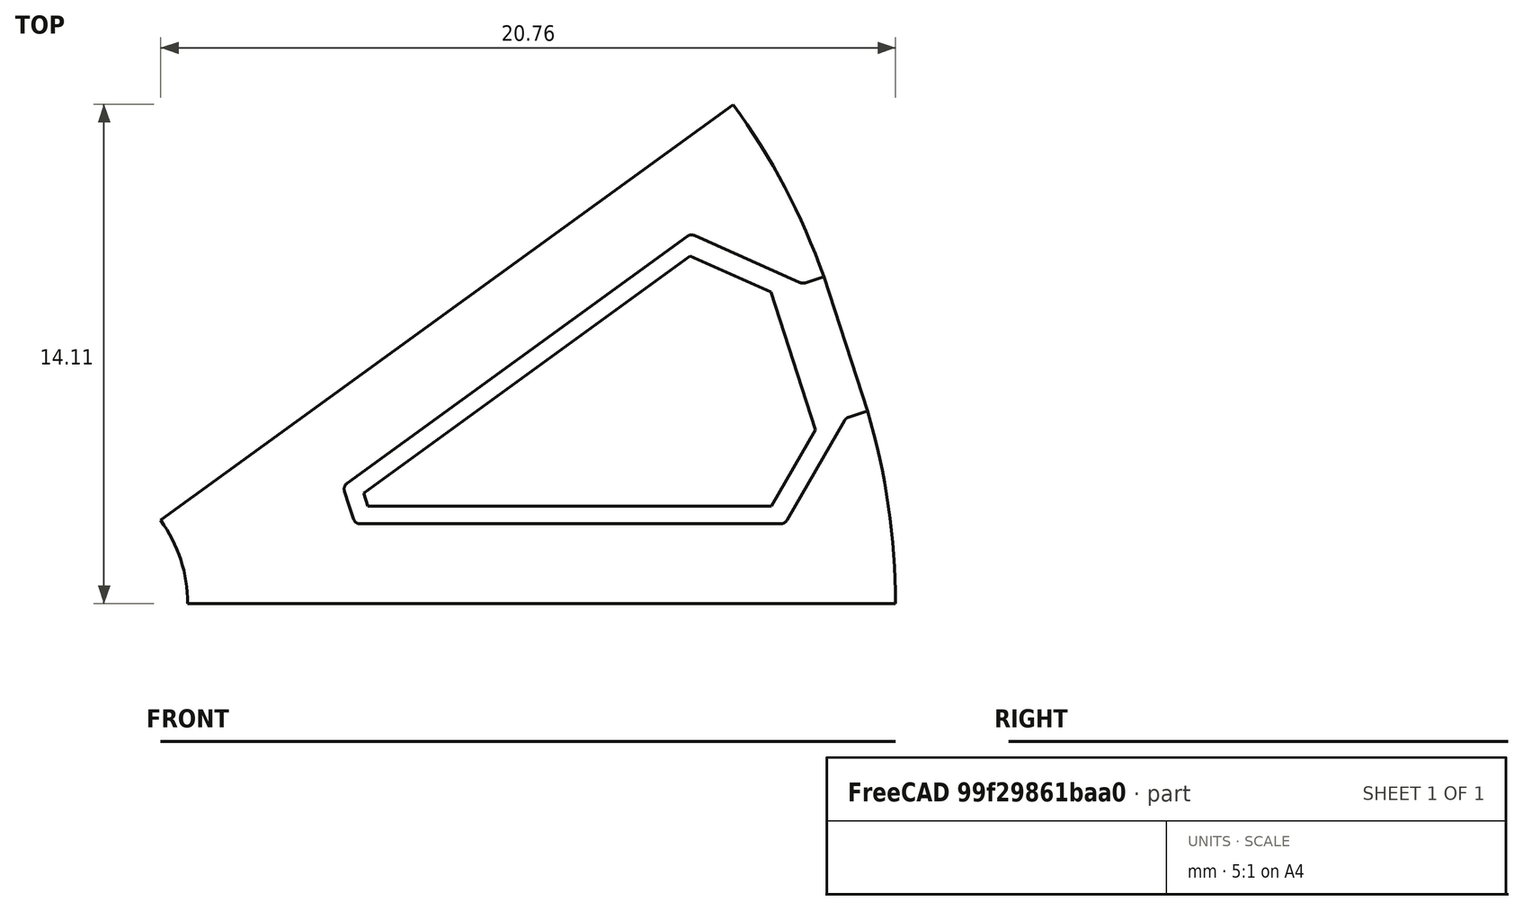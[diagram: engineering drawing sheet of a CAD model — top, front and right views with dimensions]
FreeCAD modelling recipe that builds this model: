
FCSTD DOCUMENT  (FreeCAD 0.18R4 (GitTag))
Label: stator1_new
License: All rights reserved
LicenseURL: http://en.wikipedia.org/wiki/All_rights_reserved
objects: Sketcher::SketchObject×7, Surface::Filling×3, PartDesign::Body×2, Spreadsheet::Sheet×1
note: 12 computed .brp shape members not serialized (recipe doc carries the construction recipe); baked Part::Feature solids carry a one-line shape summary decoded from their .brp

FEATURE [Spreadsheet::Sheet] Spreadsheet  label="Variables"
  cells = A2=slotNumber; B2(slotNumber)=10; A3=outerDiameter; B3(outerDiameter)=48; A4=innerDiameter; B4(innerDiameter)=8; A5=stackLength; B5(stackLength)=26; A6=stackingFactor; B6(stackingFactor)=0.95; A7=cuttingThickness; B7(cuttingThickness)=0.1; A8=skewAngle; B8(skewAngle)=0; A9=segmentAngle; B9(segmentAngle)==360 / slotNumber; A10=tipHeightReduction; B10(tipHeightReduction)=20; A11=toothThickness; B11(toothThickness)=4.5; A12=yokeThickness; B12(yokeThickness)=5; A13=tipHeight; B13(tipHeight)=0.8; A14=tipAngle; B14(tipAngle)=120; A15=openingLeft; B15(openingLeft)=2; A16=openingRight; B16(openingRight)=2; A17=slotIsolation; B17(slotIsolation)=0.5; A18=windingAngle; B18(windingAngle)=35; A19=heightRatio; B19(heightRatio)=40; A20=roundingRadii; B20(roundingRadii)=0.2; A21=coilAxialHeight; B21(coilAxialHeight)=15
FEATURE [Sketcher::SketchObject] Sketch003  label="StatorSketch"
  MapMode = 5
  Support = -> [XY_Plane]
  expr: Constraints[71] = Variables.innerDiameter / 2
  expr: Constraints[26] = Variables.toothThickness / 2
  expr: Constraints[9] = Variables.segmentAngle
  expr: Constraints[27] = Variables.innerDiameter / 2 + Variables.yokeThickness
  expr: Constraints[35] = Variables.roundingRadii
  expr: Constraints[61] = Variables.tipHeight
  expr: Constraints[23] = Variables.tipAngle
  expr: Constraints[16] = Variables.tipHeight * (1 - Variables.tipHeightReduction / 100)
  expr: Constraints[12] = Variables.openingLeft
  expr: Constraints[72] = Variables.segmentAngle / 2
  expr: Constraints[5] = Variables.outerDiameter
  sketch-geometry (29):
    g0: ArcOfCircle [constr] CenterX=0 CenterY=0 CenterZ=0 NormalX=0 NormalY=0 NormalZ=1 AngleXU=0 Radius=24 StartAngle=0 EndAngle=0.628319
    g1: LineSegment [constr] StartX=0 StartY=0 StartZ=0 EndX=19.4164 EndY=14.1068 EndZ=0
    g2: LineSegment [constr] StartX=0 StartY=0 StartZ=0 EndX=24 EndY=-7e-16 EndZ=0
    g3: LineSegment [constr] StartX=0 StartY=0 StartZ=0 EndX=22.8254 EndY=7.41641 EndZ=0
    g4: LineSegment [constr] StartX=15.6745 StartY=18.1744 StartZ=0 EndX=22.1286 EndY=9.29112 EndZ=0
    g5: LineSegment [constr] StartX=22.1286 StartY=9.29112 StartZ=0 EndX=21.4408 EndY=9.06763 EndZ=0
    g6: LineSegment [constr] StartX=21.3678 StartY=9.0439 StartZ=0 EndX=21.9764 EndY=9.24167 EndZ=0
    g7: ArcOfCircle CenterX=3.91276 CenterY=2.84278 CenterZ=0 NormalX=0 NormalY=0 NormalZ=1 AngleXU=0 Radius=19.1636 StartAngle=0.340448 EndAngle=0.628319
    g8: LineSegment StartX=21.2976 StartY=9.07513 StartZ=0 EndX=18.316 EndY=10.4026 EndZ=0
    g9: LineSegment StartX=18.1171 StartY=10.3817 StartZ=0 EndX=8.50448 EndY=3.39772 EndZ=0
    g10: LineSegment StartX=8.43183 StartY=3.17411 StartZ=0 EndX=8.55951 EndY=2.78115 EndZ=0
    g11: LineSegment [constr] StartX=8.50448 StartY=3.39772 StartZ=0 EndX=7.18197 EndY=5.218 EndZ=0
    g12: LineSegment StartX=8.55951 StartY=2.78115 StartZ=0 EndX=8.68719 EndY=2.3882 EndZ=0
    g13: LineSegment StartX=8.8774 StartY=2.25 StartZ=0 EndX=20.7593 EndY=2.25 EndZ=0
    g14: LineSegment StartX=20.9325 StartY=2.35 StartZ=0 EndX=22.5644 EndY=5.17649 EndZ=0
    g15: LineSegment StartX=22.6758 StartY=5.26671 StartZ=0 EndX=23.2114 EndY=5.44075 EndZ=0
    g16: ArcOfCircle CenterX=4.83643 CenterY=-1e-16 CenterZ=0 NormalX=0 NormalY=0 NormalZ=1 AngleXU=0 Radius=19.1636 StartAngle=0 EndAngle=0.287871
    g17: ArcOfCircle CenterX=22.7376 CenterY=5.07649 CenterZ=0 NormalX=0 NormalY=0 NormalZ=1 AngleXU=0 Radius=0.2 StartAngle=1.88496 EndAngle=2.61799
    g18: ArcOfCircle CenterX=20.7593 CenterY=2.45 CenterZ=0 NormalX=0 NormalY=0 NormalZ=1 AngleXU=0 Radius=0.2 StartAngle=4.71239 EndAngle=5.75959
    g19: ArcOfCircle CenterX=8.8774 CenterY=2.45 CenterZ=0 NormalX=0 NormalY=0 NormalZ=1 AngleXU=0 Radius=0.2 StartAngle=3.45575 EndAngle=4.71239
    g20: ArcOfCircle CenterX=18.2347 CenterY=10.2199 CenterZ=0 NormalX=0 NormalY=0 NormalZ=1 AngleXU=0 Radius=0.2 StartAngle=1.15192 EndAngle=2.19911
    g21: ArcOfCircle CenterX=21.379 CenterY=9.25784 CenterZ=0 NormalX=0 NormalY=0 NormalZ=1 AngleXU=0 Radius=0.2 StartAngle=4.29351 EndAngle=5.02655
    g22: ArcOfCircle CenterX=8.62204 CenterY=3.23591 CenterZ=0 NormalX=0 NormalY=0 NormalZ=1 AngleXU=0 Radius=0.2 StartAngle=2.19911 EndAngle=3.45575
    g23: LineSegment [constr] StartX=21.2976 StartY=9.07513 StartZ=0 EndX=21.3678 EndY=9.0439 EndZ=0
    g24: LineSegment [constr] StartX=21.3678 StartY=9.0439 StartZ=0 EndX=21.4408 EndY=9.06763 EndZ=0
    g25: LineSegment StartX=21.4408 StartY=9.06763 StartZ=0 EndX=21.9764 EndY=9.24167 EndZ=0
    g26: LineSegment StartX=19.4164 StartY=14.1068 StartZ=0 EndX=3.23607 EndY=2.35114 EndZ=0
    g27: LineSegment StartX=4 StartY=-1e-16 StartZ=0 EndX=24 EndY=-7e-16 EndZ=0
    g28: ArcOfCircle CenterX=0 CenterY=0 CenterZ=0 NormalX=0 NormalY=0 NormalZ=1 AngleXU=0 Radius=4 StartAngle=0 EndAngle=0.628319
  constraints (73):
    c: Coincident(g0,g-1)
    c: Coincident(g1,g0)
    c: Coincident(g1,g0)
    c: Coincident(g2,g0)
    c: Coincident(g2,g0)
    c: Diameter(g0) = 48
    c: Coincident(g3,g0)
    c: PointOnObject(g3,g0)
    c: Symmetric(g0,g0,g3)
    c: Angle(g2,g1) = 0.628319
    c: PointOnObject(g4,g0)
    c: Symmetric(g4,g4,g1)
    c: Distance(g4,g3) = 2
    c: Coincident(g5,g4)
    c: Parallel(g5,g3)
    c: PointOnObject(g6,g5)
    c: Distance(g6) = 0.64
    c: Coincident(g7,g0)
    c: Coincident(g7,g6)
    c: PointOnObject(g7,g1)
    c: PointOnObject(g10,g3)
    c: Perpendicular(g3,g10)
    c: Parallel(g1,g9)
    c: Angle(g9,g8) = 2.0944
    c: PointOnObject(g11,g1)
    c: Perpendicular(g1,g11)
    c: Distance(g11) = 2.25
    c: Distance(g-1,g10) = 9
    c: Coincident(g12,g10)
    c: Symmetric(g15,g7,g3)
    c: PointOnObject(g16,g2)
    c: Coincident(g16,g0)
    c: Coincident(g16,g15)
    c: Tangent(g14,g17) = 1.5708
    c: Tangent(g15,g17) = 1.5708
    c: Radius(g17) = 0.2
    c: Tangent(g13,g18) = -1.5708
    c: Tangent(g14,g18) = -1.5708
    c: Tangent(g12,g19) = -1.5708
    c: Tangent(g13,g19) = -1.5708
    c: Tangent(g8,g20) = -1.5708
    c: Tangent(g9,g20) = -1.5708
    c: Tangent(g5,g21) = 1.5708
    c: Tangent(g8,g21) = 1.5708
    c: Tangent(g10,g22) = -1.5708
    c: Tangent(g9,g22) = -1.5708
    c: Coincident(g11,g9)
    c: Equal(g17,g18)
    c: Equal(g19,g17)
    c: Equal(g22,g17)
    c: Equal(g20,g17)
    c: Symmetric(g13,g9,g3)
    c: Symmetric(g14,g8,g3)
    c: Symmetric(g14,g8,g3)
    c: Equal(g21,g17)
    c: Coincident(g23,g8)
    c: Coincident(g24,g23)
    c: Coincident(g24,g5)
    c: Parallel(g23,g8)
    c: Parallel(g24,g5)
    c: Coincident(g6,g23)
    c: Distance(g6,g4) = 0.8
    c: Coincident(g25,g21)
    c: Coincident(g25,g7)
    c: Coincident(g26,g7)
    c: PointOnObject(g26,g1)
    c: PointOnObject(g27,g2)
    c: Coincident(g27,g16)
    c: Coincident(g28,g-1)
    c: Coincident(g28,g26)
    c: Coincident(g28,g27)
    c: Radius(g28) = 4
    c: Angle(g-1,g3) = 0.314159
FEATURE [Sketcher::SketchObject] Sketch  label="StatorSide"
  MapMode = 5
  Support = -> [XY_Plane001]
  expr: Constraints[20] = Variables.stackLength
  expr: Constraints[17] = Variables.innerDiameter
  expr: Constraints[16] = Variables.outerDiameter
  sketch-geometry (8):
    g0: LineSegment StartX=-13 StartY=24 StartZ=0 EndX=13 EndY=24 EndZ=0
    g1: LineSegment StartX=13 StartY=24 StartZ=0 EndX=13 EndY=4 EndZ=0
    g2: LineSegment StartX=13 StartY=4 StartZ=0 EndX=-13 EndY=4 EndZ=0
    g3: LineSegment StartX=-13 StartY=4 StartZ=0 EndX=-13 EndY=24 EndZ=0
    g4: LineSegment StartX=-13 StartY=-4 StartZ=0 EndX=13 EndY=-4 EndZ=0
    g5: LineSegment StartX=13 StartY=-4 StartZ=0 EndX=13 EndY=-24 EndZ=0
    g6: LineSegment StartX=13 StartY=-24 StartZ=0 EndX=-13 EndY=-24 EndZ=0
    g7: LineSegment StartX=-13 StartY=-24 StartZ=0 EndX=-13 EndY=-4 EndZ=0
  constraints (21):
    c: Coincident(g0,g1)
    c: Coincident(g1,g2)
    c: Coincident(g2,g3)
    c: Coincident(g3,g0)
    c: Horizontal(g0)
    c: Vertical(g1)
    c: Vertical(g3)
    c: Coincident(g4,g5)
    c: Coincident(g5,g6)
    c: Coincident(g6,g7)
    c: Coincident(g7,g4)
    c: Horizontal(g6)
    c: Vertical(g5)
    c: Vertical(g7)
    c: Symmetric(g2,g1,g-2)
    c: Symmetric(g4,g4,g-2)
    c: DistanceY(g6,g0) = 48
    c: DistanceY(g4,g2) = 8
    c: Symmetric(g4,g2,g-1)
    c: Equal(g7,g3)
    c: DistanceX(g6,g6) = 26
FEATURE [Sketcher::SketchObject] Sketch009  label="WindingSide"
  ExternalGeometry = -> [Sketch]
  MapMode = 5
  Support = -> [XY_Plane001]
  expr: Constraints[18] = Variables.coilAxialHeight
  expr: Constraints[8] = Variables.coilAxialHeight
  sketch-geometry (12):
    g0: ArcOfEllipse CenterX=-13 CenterY=0 CenterZ=0 NormalX=0 NormalY=0 NormalZ=1 MajorRadius=24 MinorRadius=15 AngleXU=1.5708 StartAngle=1e-16 EndAngle=3.14159
    g1: LineSegment [constr] StartX=-13 StartY=24 StartZ=0 EndX=-13 EndY=-24 EndZ=0
    g2: LineSegment [constr] StartX=-28 StartY=0 StartZ=0 EndX=2 EndY=0 EndZ=0
    g3: GeomPoint X=-13 Y=18.735 Z=0
    g4: GeomPoint X=-13 Y=-18.735 Z=0
    g5: LineSegment StartX=-13 StartY=24 StartZ=0 EndX=-13 EndY=-24 EndZ=0
    g6: ArcOfEllipse CenterX=13 CenterY=0 CenterZ=0 NormalX=0 NormalY=0 NormalZ=1 MajorRadius=24 MinorRadius=15 AngleXU=-1.5708 StartAngle=0 EndAngle=3.14159
    g7: LineSegment [constr] StartX=13 StartY=-24 StartZ=0 EndX=13 EndY=24 EndZ=0
    g8: LineSegment [constr] StartX=28 StartY=0 StartZ=0 EndX=-2 EndY=0 EndZ=0
    g9: GeomPoint X=13 Y=-18.735 Z=0
    g10: GeomPoint X=13 Y=18.735 Z=0
    g11: LineSegment StartX=13 StartY=24 StartZ=0 EndX=13 EndY=-24 EndZ=0
  constraints (18):
    c: InternalAlignment(g1-g4 -> g0) x4
    c: PointOnObject(g0,g-4)
    c: Horizontal(g2)
    c: PointOnObject(g0,g-1)
    c: PointOnObject(g1,g-3)
    c: DistanceX(g2,g0) = 15
    c: Coincident(g0,g-3)
    c: Coincident(g5,g0)
    c: Coincident(g5,g0)
    c: InternalAlignment(g7-g10 -> g6) x4
    c: PointOnObject(g6,g-1)
    c: Coincident(g6,g-6)
    c: DistanceX(g6,g8) = 15
    c: Coincident(g6,g7)
    c: Horizontal(g8)
    c: PointOnObject(g6,g7)
    c: Coincident(g11,g6)
    c: Coincident(g11,g6)
FEATURE [PartDesign::Body] Body001  label="SideView"
  Group = -> [Sketch,Sketch009]
  Origin = -> Origin001
FEATURE [Sketcher::SketchObject] Sketch011  label="TerminalSketch"
  ExternalGeometry = -> [Sketch003]
  MapMode = 5
  Support = -> [XY_Plane]
  expr: Constraints[17] = Variables.innerDiameter / 2 + Variables.yokeThickness + Variables.slotIsolation
  expr: Constraints[31] = Variables.slotIsolation
  expr: Constraints[28] = 90
  expr: Constraints[18] = Variables.toothThickness / 2 + Variables.slotIsolation
  expr: Constraints[2] = (Variables.outerDiameter / 2 - Variables.innerDiameter / 2 - Variables.yokeThickness - Variables.tipHeight) * Variables.heightRatio / 100
  sketch-geometry (12):
    g0: LineSegment [constr] StartX=8.55951 StartY=2.78115 StartZ=0 EndX=13.9615 EndY=4.53637 EndZ=0
    g1: LineSegment StartX=20.477 StartY=8.8085 StartZ=0 EndX=18.1986 EndY=9.8229 EndZ=0
    g2: LineSegment StartX=18.1986 StartY=9.8229 StartZ=0 EndX=8.97471 EndY=3.12132 EndZ=0
    g3: LineSegment StartX=8.97471 StartY=3.12132 StartZ=0 EndX=9.09536 EndY=2.75 EndZ=0
    g4: LineSegment StartX=9.09536 StartY=2.75 StartZ=0 EndX=20.4968 EndY=2.75 EndZ=0
    g5: LineSegment StartX=20.4968 StartY=2.75 StartZ=0 EndX=21.7438 EndY=4.90986 EndZ=0
    g6: LineSegment StartX=21.7438 StartY=4.90986 StartZ=0 EndX=20.477 EndY=8.8085 EndZ=0
    g7: GeomPoint X=9.03504 Y=2.93566 Z=0
    g8: LineSegment [constr] StartX=22.5644 StartY=5.17649 StartZ=0 EndX=21.2976 EndY=9.07513 EndZ=0
    g9: LineSegment [constr] StartX=18.1986 StartY=9.8229 StartZ=0 EndX=17.6712 EndY=10.0577 EndZ=0
    g10: LineSegment [constr] StartX=18.1986 StartY=9.8229 StartZ=0 EndX=18.4335 EndY=10.3503 EndZ=0
    g11: LineSegment [constr] StartX=13.7237 StartY=4.45912 StartZ=0 EndX=14.1993 EndY=4.61362 EndZ=0
  constraints (32):
    c: Coincident(g0,g-6)
    c: Perpendicular(g0,g-5)
    c: Distance(g0) = 5.68
    c: Coincident(g1,g2)
    c: Coincident(g2,g3)
    c: Coincident(g3,g4)
    c: Horizontal(g4)
    c: Coincident(g4,g5)
    c: Coincident(g5,g6)
    c: Coincident(g6,g1)
    c: Parallel(g1,g-3)
    c: Parallel(g5,g-8)
    c: Parallel(g6,g3)
    c: Symmetric(g3,g2,g0)
    c: Symmetric(g4,g1,g0)
    c: PointOnObject(g7,g3)
    c: PointOnObject(g7,g0)
    c: Distance(g-1,g7) = 9.5
    c: DistanceY(g-1,g3) = 2.75
    c: Coincident(g8,g-8)
    c: Coincident(g8,g-3)
    c: Equal(g8,g6)
    c: Coincident(g9,g1)
    c: PointOnObject(g9,g-4)
    c: Coincident(g10,g1)
    c: PointOnObject(g10,g-3)
    c: Angle(g10,g9) = 1.5708
    c: Equal(g9,g10)
    c: Angle(g1,g10) = 1.5708
    c: PointOnObject(g11,g0)
    c: Symmetric(g11,g11,g0)
    c: Distance(g11,g11) = 0.5
FEATURE [Sketcher::SketchObject] Sketch013  label="YokeLine"
  ExternalGeometry = -> [Sketch003]
  MapMode = 5
  Support = -> [XY_Plane]
  sketch-geometry (1):
    g0: LineSegment StartX=8.55951 StartY=2.78115 StartZ=0 EndX=3.80423 EndY=1.23607 EndZ=0
  constraints (3):
    c: Coincident(g0,g-4)
    c: PointOnObject(g0,g-3)
    c: Angle(g-4,g0) = 1.5708
FEATURE [Sketcher::SketchObject] Sketch014  label="ToothLine"
  ExternalGeometry = -> [Sketch003]
  MapMode = 5
  Support = -> [XY_Plane]
  expr: Constraints[2] = Variables.toothThickness
  sketch-geometry (1):
    g0: LineSegment StartX=13.3108 StartY=6.88971 StartZ=0 EndX=10.6658 EndY=10.5303 EndZ=0
  constraints (3):
    c: Symmetric(g-3,g-3,g0)
    c: Angle(g-3,g0) = 1.5708
    c: Distance(g0) = 4.5
FEATURE [Surface::Filling] Surface  label="StatorSketch_Surface"
  Anisotropy = false
  BoundaryEdges = -> [Sketch003]
  BoundaryOrder = [0,0,0,0,0,0,0,0,0,0,0,0,0,0,0,0,0,0,0]
  Degree = 3
  Iterations = 2
  MaximumDegree = 8
  MaximumSegments = 9
  PointsOnCurve = 15
  TolAngular = 0.01
  TolCurvature = 0.1
  Tolerance2d = 1e-05
  Tolerance3d = 0.0001
FEATURE [Surface::Filling] Surface001  label="TerminalSketch_Surface"
  Anisotropy = false
  BoundaryEdges = -> [Sketch011]
  BoundaryOrder = [0,0,0,0,0,0]
  Degree = 3
  Iterations = 2
  MaximumDegree = 8
  MaximumSegments = 9
  PointsOnCurve = 15
  TolAngular = 0.01
  TolCurvature = 0.1
  Tolerance2d = 1e-05
  Tolerance3d = 0.0001
FEATURE [Sketcher::SketchObject] Sketch015  label="SlotSketch"
  MapMode = 5
  Support = -> [XY_Plane]
  expr: Constraints[71] = Variables.innerDiameter / 2
  expr: Constraints[26] = Variables.toothThickness / 2
  expr: Constraints[9] = Variables.segmentAngle
  expr: Constraints[27] = Variables.innerDiameter / 2 + Variables.yokeThickness
  expr: Constraints[35] = Variables.roundingRadii
  expr: Constraints[61] = Variables.tipHeight
  expr: Constraints[23] = Variables.tipAngle
  expr: Constraints[16] = Variables.tipHeight * (1 - Variables.tipHeightReduction / 100)
  expr: Constraints[12] = Variables.openingLeft
  expr: Constraints[72] = Variables.segmentAngle / 2
  expr: Constraints[5] = Variables.outerDiameter
  sketch-geometry (30):
    g0: ArcOfCircle [constr] CenterX=0 CenterY=0 CenterZ=0 NormalX=0 NormalY=0 NormalZ=1 AngleXU=0 Radius=24 StartAngle=0 EndAngle=0.628319
    g1: LineSegment [constr] StartX=0 StartY=0 StartZ=0 EndX=19.4164 EndY=14.1068 EndZ=0
    g2: LineSegment [constr] StartX=0 StartY=0 StartZ=0 EndX=24 EndY=9e-16 EndZ=0
    g3: LineSegment [constr] StartX=0 StartY=0 StartZ=0 EndX=22.8254 EndY=7.41641 EndZ=0
    g4: LineSegment [constr] StartX=15.6745 StartY=18.1744 StartZ=0 EndX=22.1286 EndY=9.29112 EndZ=0
    g5: LineSegment [constr] StartX=22.1286 StartY=9.29112 StartZ=0 EndX=21.4408 EndY=9.06763 EndZ=0
    g6: LineSegment [constr] StartX=21.3678 StartY=9.0439 StartZ=0 EndX=21.9764 EndY=9.24167 EndZ=0
    g7: ArcOfCircle [constr] CenterX=3.91276 CenterY=2.84278 CenterZ=0 NormalX=0 NormalY=0 NormalZ=1 AngleXU=0 Radius=19.1636 StartAngle=0.340448 EndAngle=0.628319
    g8: LineSegment StartX=21.2976 StartY=9.07513 StartZ=0 EndX=18.316 EndY=10.4026 EndZ=0
    g9: LineSegment StartX=18.1171 StartY=10.3817 StartZ=0 EndX=8.50448 EndY=3.39772 EndZ=0
    g10: LineSegment StartX=8.43183 StartY=3.17411 StartZ=0 EndX=8.55951 EndY=2.78115 EndZ=0
    g11: LineSegment [constr] StartX=8.50448 StartY=3.39772 StartZ=0 EndX=7.18197 EndY=5.218 EndZ=0
    g12: LineSegment StartX=8.55951 StartY=2.78115 StartZ=0 EndX=8.68719 EndY=2.3882 EndZ=0
    g13: LineSegment StartX=8.8774 StartY=2.25 StartZ=0 EndX=20.7593 EndY=2.25 EndZ=0
    g14: LineSegment StartX=20.9325 StartY=2.35 StartZ=0 EndX=22.5644 EndY=5.17649 EndZ=0
    g15: LineSegment StartX=22.6758 StartY=5.26671 StartZ=0 EndX=23.2114 EndY=5.44075 EndZ=0
    g16: ArcOfCircle [constr] CenterX=4.83643 CenterY=2e-16 CenterZ=0 NormalX=0 NormalY=0 NormalZ=1 AngleXU=0 Radius=19.1636 StartAngle=0 EndAngle=0.287871
    g17: ArcOfCircle CenterX=22.7376 CenterY=5.07649 CenterZ=0 NormalX=0 NormalY=0 NormalZ=1 AngleXU=0 Radius=0.2 StartAngle=1.88496 EndAngle=2.61799
    g18: ArcOfCircle CenterX=20.7593 CenterY=2.45 CenterZ=0 NormalX=0 NormalY=0 NormalZ=1 AngleXU=0 Radius=0.2 StartAngle=4.71239 EndAngle=5.75959
    g19: ArcOfCircle CenterX=8.8774 CenterY=2.45 CenterZ=0 NormalX=0 NormalY=0 NormalZ=1 AngleXU=0 Radius=0.2 StartAngle=3.45575 EndAngle=4.71239
    g20: ArcOfCircle CenterX=18.2347 CenterY=10.2199 CenterZ=0 NormalX=0 NormalY=0 NormalZ=1 AngleXU=0 Radius=0.2 StartAngle=1.15192 EndAngle=2.19911
    g21: ArcOfCircle CenterX=21.379 CenterY=9.25784 CenterZ=0 NormalX=0 NormalY=0 NormalZ=1 AngleXU=0 Radius=0.2 StartAngle=4.29351 EndAngle=5.02655
    g22: ArcOfCircle CenterX=8.62204 CenterY=3.23591 CenterZ=0 NormalX=0 NormalY=0 NormalZ=1 AngleXU=0 Radius=0.2 StartAngle=2.19911 EndAngle=3.45575
    g23: LineSegment [constr] StartX=21.2976 StartY=9.07513 StartZ=0 EndX=21.3678 EndY=9.0439 EndZ=0
    g24: LineSegment [constr] StartX=21.3678 StartY=9.0439 StartZ=0 EndX=21.4408 EndY=9.06763 EndZ=0
    g25: LineSegment StartX=21.4408 StartY=9.06763 StartZ=0 EndX=21.9764 EndY=9.24167 EndZ=0
    g26: LineSegment [constr] StartX=19.4164 StartY=14.1068 StartZ=0 EndX=3.23607 EndY=2.35114 EndZ=0
    g27: LineSegment [constr] StartX=4 StartY=1e-16 StartZ=0 EndX=24 EndY=9e-16 EndZ=0
    g28: ArcOfCircle [constr] CenterX=0 CenterY=0 CenterZ=0 NormalX=0 NormalY=0 NormalZ=1 AngleXU=0 Radius=4 StartAngle=0 EndAngle=0.628319
    g29: LineSegment StartX=21.9764 StartY=9.24167 StartZ=0 EndX=23.2114 EndY=5.44075 EndZ=0
  constraints (75):
    c: Coincident(g0,g-1)
    c: Coincident(g1,g0)
    c: Coincident(g1,g0)
    c: Coincident(g2,g0)
    c: Coincident(g2,g0)
    c: Diameter(g0) = 48
    c: Coincident(g3,g0)
    c: PointOnObject(g3,g0)
    c: Symmetric(g0,g0,g3)
    c: Angle(g2,g1) = 0.628319
    c: PointOnObject(g4,g0)
    c: Symmetric(g4,g4,g1)
    c: Distance(g4,g3) = 2
    c: Coincident(g5,g4)
    c: Parallel(g5,g3)
    c: PointOnObject(g6,g5)
    c: Distance(g6) = 0.64
    c: Coincident(g7,g0)
    c: Coincident(g7,g6)
    c: PointOnObject(g7,g1)
    c: PointOnObject(g10,g3)
    c: Perpendicular(g3,g10)
    c: Parallel(g1,g9)
    c: Angle(g9,g8) = 2.0944
    c: PointOnObject(g11,g1)
    c: Perpendicular(g1,g11)
    c: Distance(g11) = 2.25
    c: Distance(g-1,g10) = 9
    c: Coincident(g12,g10)
    c: Symmetric(g15,g7,g3)
    c: PointOnObject(g16,g2)
    c: Coincident(g16,g0)
    c: Coincident(g16,g15)
    c: Tangent(g14,g17) = 1.5708
    c: Tangent(g15,g17) = 1.5708
    c: Radius(g17) = 0.2
    c: Tangent(g13,g18) = -1.5708
    c: Tangent(g14,g18) = -1.5708
    c: Tangent(g12,g19) = -1.5708
    c: Tangent(g13,g19) = -1.5708
    c: Tangent(g8,g20) = -1.5708
    c: Tangent(g9,g20) = -1.5708
    c: Tangent(g5,g21) = 1.5708
    c: Tangent(g8,g21) = 1.5708
    c: Tangent(g10,g22) = -1.5708
    c: Tangent(g9,g22) = -1.5708
    c: Coincident(g11,g9)
    c: Equal(g17,g18)
    c: Equal(g19,g17)
    c: Equal(g22,g17)
    c: Equal(g20,g17)
    c: Symmetric(g13,g9,g3)
    c: Symmetric(g14,g8,g3)
    c: Symmetric(g14,g8,g3)
    c: Equal(g21,g17)
    c: Coincident(g23,g8)
    c: Coincident(g24,g23)
    c: Coincident(g24,g5)
    c: Parallel(g23,g8)
    c: Parallel(g24,g5)
    c: Coincident(g6,g23)
    c: Distance(g6,g4) = 0.8
    c: Coincident(g25,g21)
    c: Coincident(g25,g7)
    c: Coincident(g26,g7)
    c: PointOnObject(g26,g1)
    c: PointOnObject(g27,g2)
    c: Coincident(g27,g16)
    c: Coincident(g28,g-1)
    c: Coincident(g28,g26)
    c: Coincident(g28,g27)
    c: Radius(g28) = 4
    c: Angle(g-1,g3) = 0.314159
    c: Coincident(g29,g25)
    c: Coincident(g29,g15)
FEATURE [PartDesign::Body] Body  label="TopView"
  Group = -> [Sketch003,Sketch011,Sketch013,Sketch014,Sketch015]
  Origin = -> Origin
FEATURE [Surface::Filling] Surface002  label="SlotSketch_Surface"
  Anisotropy = false
  BoundaryEdges = -> [Sketch015]
  BoundaryOrder = [0,0,0,0,0,0,0,0,0,0,0,0,0,0,0]
  Degree = 3
  Iterations = 2
  MaximumDegree = 8
  MaximumSegments = 9
  PointsOnCurve = 15
  TolAngular = 0.01
  TolCurvature = 0.1
  Tolerance2d = 1e-05
  Tolerance3d = 0.0001
